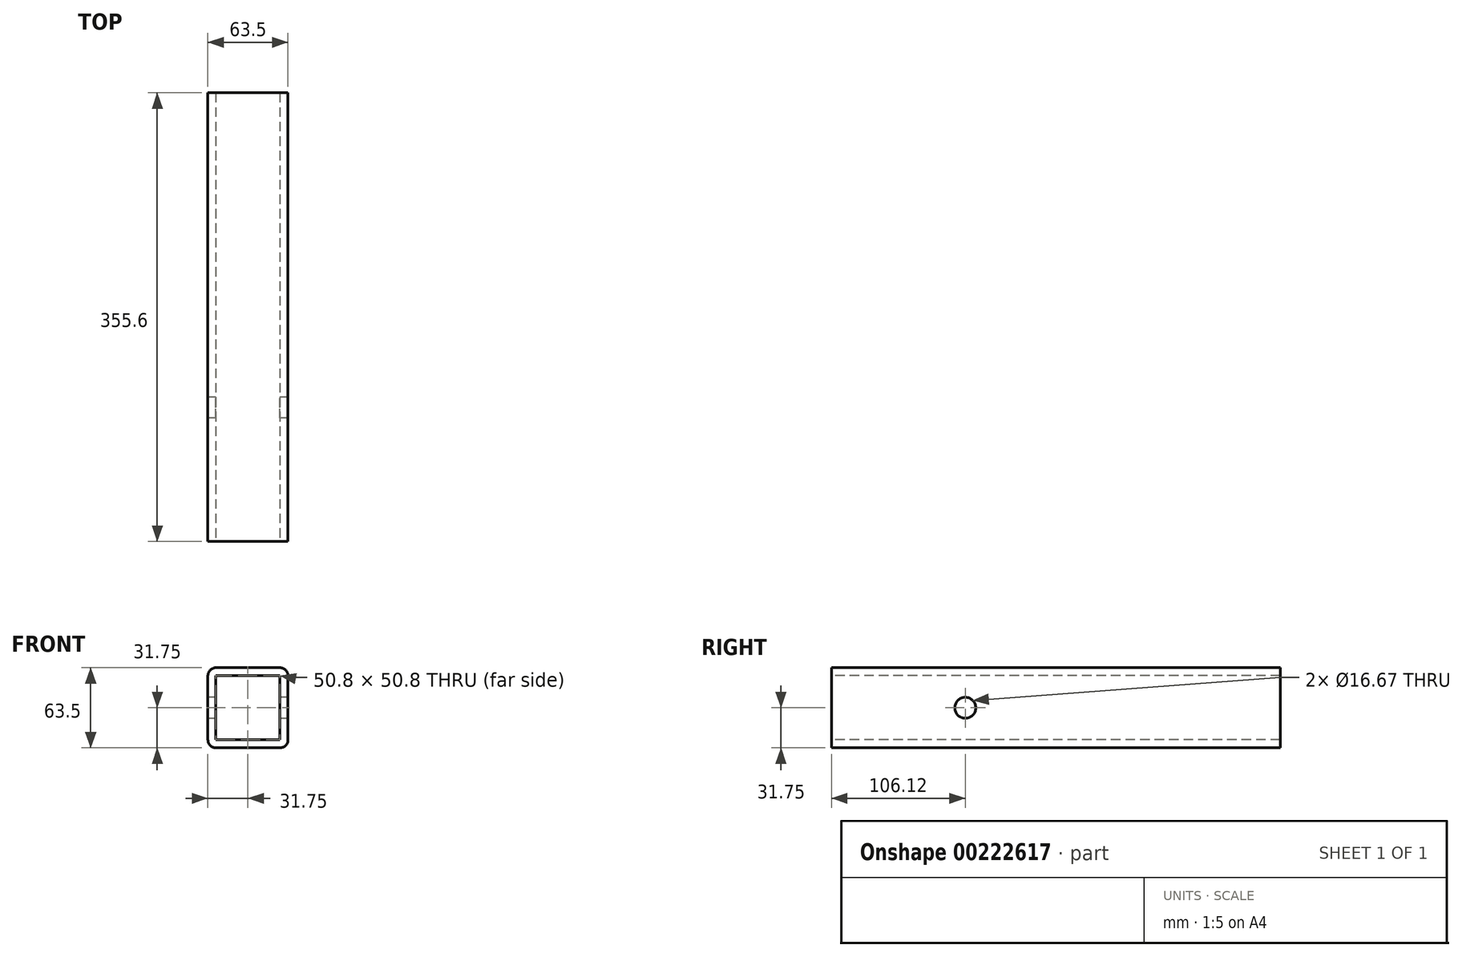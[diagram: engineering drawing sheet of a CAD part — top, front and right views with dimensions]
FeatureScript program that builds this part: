
annotation { "Feature Type Name" : "Feature", "Feature Type Description" : "" }
export const myFeature = defineFeature(function(context is Context, id is Id, definition is map)
    precondition{}
    {
        {
            var Q0;
            Q0=qCreatedBy(makeId("Front.planeOp"),FACE);
            var sketch = newSketch(context, id + "F0", { "sketchPlane" : qUnion([Q0])});
            skLineSegment(sketch, "E0.bottom", {"start": v(-25.4, 25.4) * mm, "end": v(25.4, 25.4) * mm});
            skLineSegment(sketch, "E0.top", {"start": v(-25.4, -25.4) * mm, "end": v(25.4, -25.4) * mm});
            skLineSegment(sketch, "E0.left", {"start": v(-25.4, 25.4) * mm, "end": v(-25.4, -25.4) * mm});
            skLineSegment(sketch, "E0.right", {"start": v(25.4, 25.4) * mm, "end": v(25.4, -25.4) * mm});
            skPoint(sketch, "E0.middle", {"position": v(0, 0) * mm});
            skLineSegment(sketch, "E1.0", {"start": v(-25.4, 31.75) * mm, "end": v(25.4, 31.75) * mm});
            skLineSegment(sketch, "E1.1", {"start": v(-31.75, 25.4) * mm, "end": v(-31.75, -25.4) * mm});
            skLineSegment(sketch, "E1.2", {"start": v(-25.4, -31.75) * mm, "end": v(25.4, -31.75) * mm});
            skLineSegment(sketch, "E1.3", {"start": v(31.75, 25.4) * mm, "end": v(31.75, -25.4) * mm});
            skPoint(sketch, "E2.visualSharp", {"position": v(-31.75, 31.75) * mm});
            skArc(sketch, "E2.filletArc", {"start": v(-25.4, 31.75) * mm, "mid": v(-29.9, 29.9) * mm, "end": v(-31.75, 25.4) * mm});
            skPoint(sketch, "E3.visualSharp", {"position": v(31.75, 31.75) * mm});
            skArc(sketch, "E3.filletArc", {"start": v(31.75, 25.4) * mm, "mid": v(29.9, 29.9) * mm, "end": v(25.4, 31.75) * mm});
            skPoint(sketch, "E4.visualSharp", {"position": v(31.75, -31.75) * mm});
            skArc(sketch, "E4.filletArc", {"start": v(25.4, -31.75) * mm, "mid": v(29.9, -29.9) * mm, "end": v(31.75, -25.4) * mm});
            skPoint(sketch, "E5.visualSharp", {"position": v(-31.75, -31.75) * mm});
            skArc(sketch, "E5.filletArc", {"start": v(-31.75, -25.4) * mm, "mid": v(-29.9, -29.9) * mm, "end": v(-25.4, -31.75) * mm});
            skSolve(sketch);
        }
        {
            var Q0;
            Q0 = qSketchRegion(id + "F0", true);
            extrude(context, id + "F1", {"entities" : qUnion([Q0]), "oppositeDirection" : true, "depth" : 330.2 * mm});
        }
        {
            var Q0;
            Q0=makeQuery(id+"F0.imprint","IMPRINT",FACE,{"disambiguationData":[TD([[makeQuery(id+"F0.imprint","IMPRINT",EDGE,{"derivedFrom":sQuery(id+"F0.wireOp",EDGE,"E0.bottom")}),1.0]])]});
            extrude(context, id + "F2", {"entities" : qUnion([Q0]), "operationType" : NewBodyOperationType.ADD, "depth" : 25.4 * mm});
        }
        {
            var Q0;
            {var subQ0=sQuery(id+"F0.wireOp",EDGE,"E1.1");Q0=makeQuery(id+"F2.boolean.opBoolean","MERGE",FACE,{"derivedFrom":[makeQuery(id+"F1.opExtrude","SWEPT_FACE",FACE,{"disambiguationData":[OSD([subQ0])]}),makeQuery(id+"F2.opExtrude","SWEPT_FACE",FACE,{"disambiguationData":[OSD([subQ0])]})]});}
            var sketch = newSketch(context, id + "F3", { "sketchPlane" : qUnion([Q0])});
            skCircle(sketch, "E6", {"center": v(-80.72, 0) * mm, "radius": 7.94 * mm});
            skSolve(sketch);
        }
        {
            var Q0;
            Q0=sQuery(id+"F3.wireOp",VERTEX,"E6.center");
            var Q1;
            Q1=makeQuery(id+"F1.opExtrude","SWEPT_BODY",BODY,{"disambiguationData":[OSD([sQuery(id+"F0.wireOp",EDGE,"E0.bottom"),sQuery(id+"F0.wireOp",EDGE,"E0.top"),sQuery(id+"F0.wireOp",EDGE,"E0.left"),sQuery(id+"F0.wireOp",EDGE,"E0.right"),sQuery(id+"F0.wireOp",EDGE,"E1.0"),sQuery(id+"F0.wireOp",EDGE,"E1.1"),sQuery(id+"F0.wireOp",EDGE,"E1.2"),sQuery(id+"F0.wireOp",EDGE,"E1.3"),sQuery(id+"F0.wireOp",EDGE,"E2.filletArc"),sQuery(id+"F0.wireOp",EDGE,"E3.filletArc"),sQuery(id+"F0.wireOp",EDGE,"E4.filletArc"),sQuery(id+"F0.wireOp",EDGE,"E5.filletArc")])]});
            hole(context, id + "F4", {"style" : HoleStyle.SIMPLE, "endStyle" : HoleEndStyle.THROUGH, "standardTappedOrClearance" : lookupTablePath({ "standard" : "ANSI", "fit" : "Normal (ASME)", "size" : "5/8", "type" : "Clearance" }), "standardBlindInLast" : lookupTablePath({ "fit" : "Free", "standard" : "ANSI", "size" : "5/8", "type" : "Clearance" }), "holeDiameter" : 16.67 * mm, "locations" : qUnion([Q0]), "scope" : qUnion([Q1]), "isTappedThrough" : true});
        }
    });
